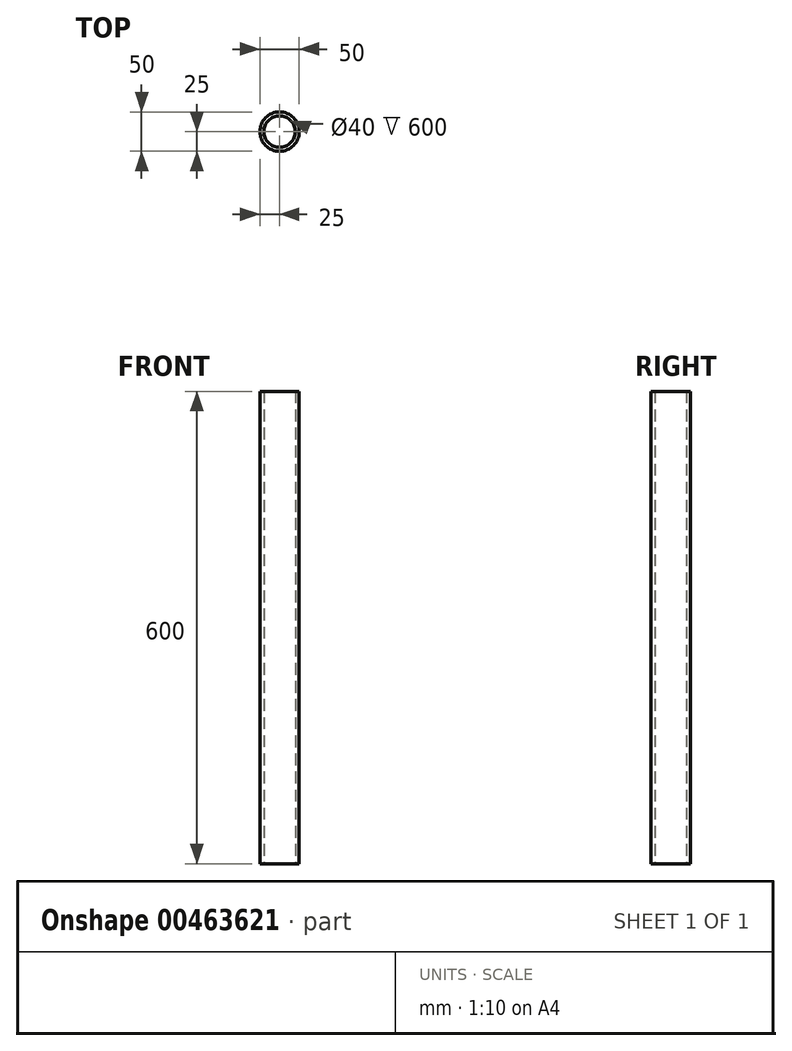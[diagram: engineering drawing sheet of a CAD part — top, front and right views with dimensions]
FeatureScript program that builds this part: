
annotation { "Feature Type Name" : "Feature", "Feature Type Description" : "" }
export const myFeature = defineFeature(function(context is Context, id is Id, definition is map)
    precondition{}
    {
        {
            var Q0;
            Q0=qCreatedBy(makeId("Top.planeOp"),FACE);
            var sketch = newSketch(context, id + "F0", { "sketchPlane" : qUnion([Q0])});
            skCircle(sketch, "E0", {"center": v(0, 0) * mm, "radius": 25 * mm});
            skCircle(sketch, "E1", {"center": v(0, 0) * mm, "radius": 20 * mm});
            skSolve(sketch);
        }
        {
            var Q0;
            Q0=makeQuery(id+"F0.imprint","IMPRINT",FACE,{"disambiguationData":[TD([[makeQuery(id+"F0.imprint","IMPRINT",EDGE,{"derivedFrom":sQuery(id+"F0.wireOp",EDGE,"E0")}),1.0]])]});
            extrude(context, id + "F1", {"entities" : qUnion([Q0]), "depth" : 600 * mm});
        }
    });
